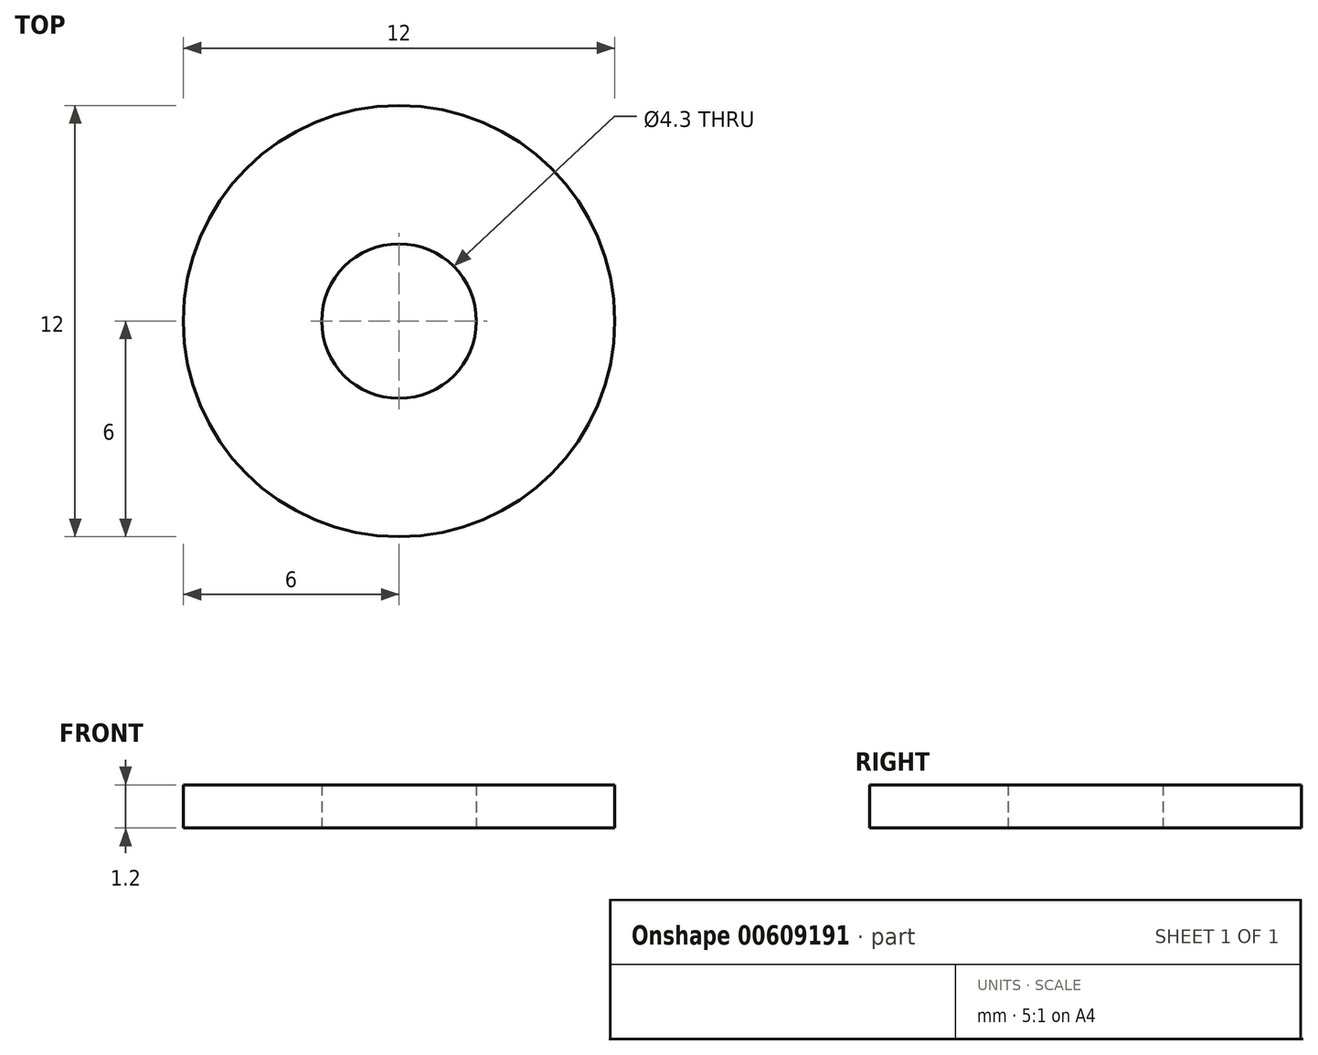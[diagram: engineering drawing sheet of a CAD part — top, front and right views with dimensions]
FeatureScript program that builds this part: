
annotation { "Feature Type Name" : "Feature", "Feature Type Description" : "" }
export const myFeature = defineFeature(function(context is Context, id is Id, definition is map)
    precondition{}
    {
        {
            var Q0;
            Q0=qCreatedBy(makeId("Top.planeOp"),FACE);
            var sketch = newSketch(context, id + "F0", { "sketchPlane" : qUnion([Q0])});
            skCircle(sketch, "E0", {"center": v(0, 0) * mm, "radius": 2.15 * mm});
            skCircle(sketch, "E1", {"center": v(0, 0) * mm, "radius": 6 * mm});
            skSolve(sketch);
        }
        {
            var Q0;
            Q0 = qSketchRegion(id + "F0", true);
            extrude(context, id + "F1", {"entities" : qUnion([Q0]), "depth" : 1.2 * mm, "offsetDistance" : 25 * mm});
        }
    });
